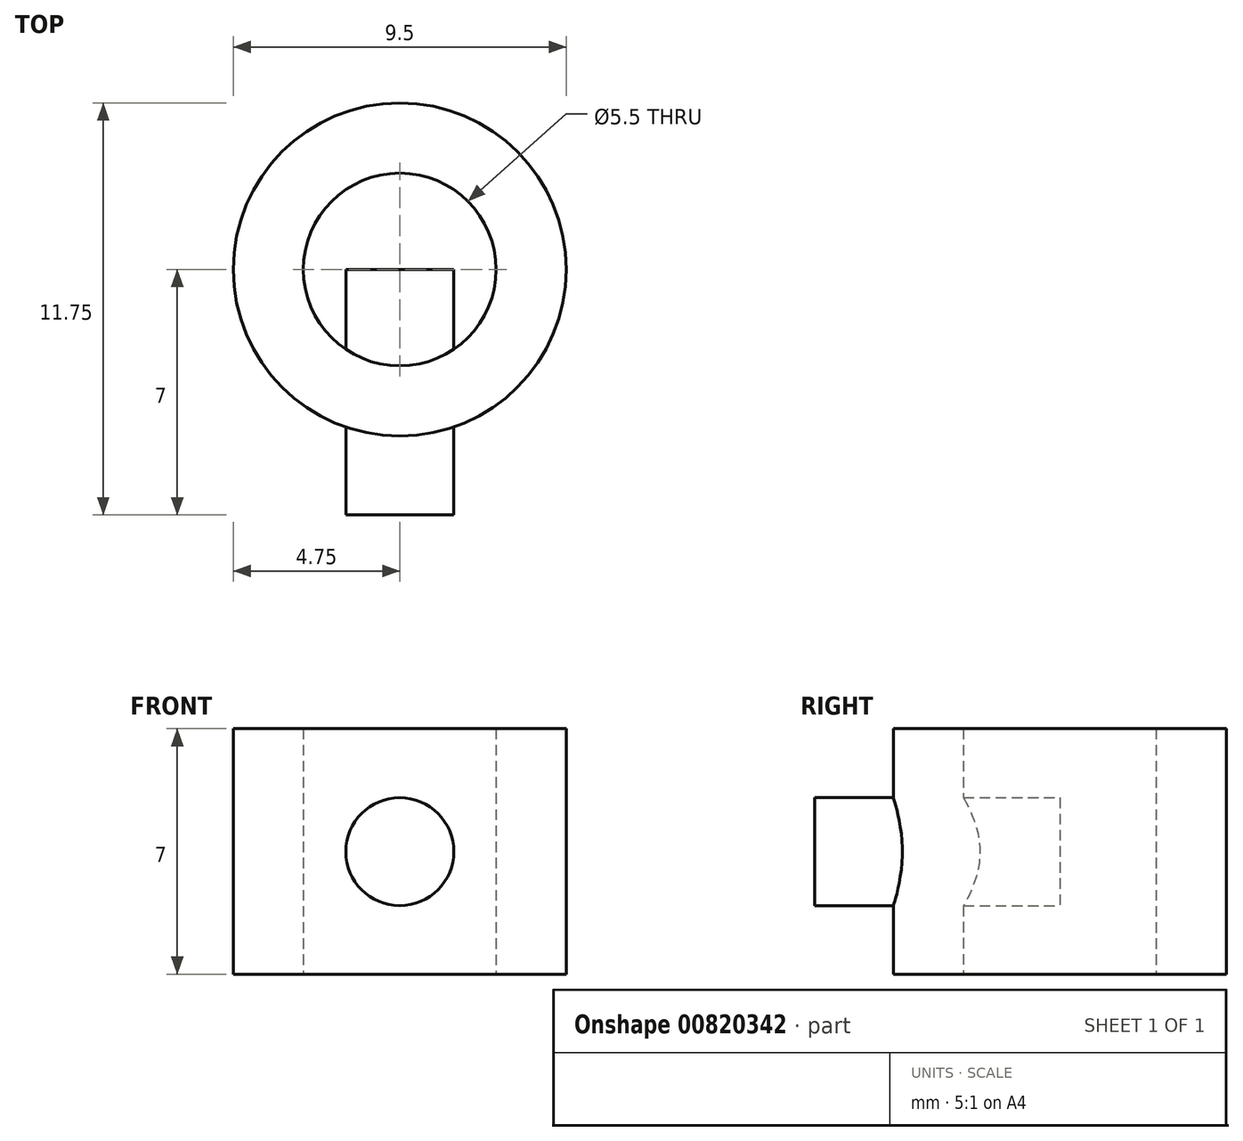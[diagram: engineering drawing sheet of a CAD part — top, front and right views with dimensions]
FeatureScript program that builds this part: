
annotation { "Feature Type Name" : "Feature", "Feature Type Description" : "" }
export const myFeature = defineFeature(function(context is Context, id is Id, definition is map)
    precondition{}
    {
        {
            var Q0;
            Q0=qCreatedBy(makeId("Top.planeOp"),FACE);
            var sketch = newSketch(context, id + "F0", { "sketchPlane" : qUnion([Q0])});
            skCircle(sketch, "E0", {"center": v(0, 0) * mm, "radius": 2.75 * mm});
            skCircle(sketch, "E1.0", {"center": v(0, 0) * mm, "radius": 4.75 * mm});
            skSolve(sketch);
        }
        {
            var Q0;
            Q0 = qSketchRegion(id + "F0", true);
            extrude(context, id + "F1", {"entities" : qUnion([Q0]), "depth" : 7 * mm, "offsetDistance" : 25 * mm});
        }
        {
            var Q0;
            Q0=qCreatedBy(makeId("Front.planeOp"),FACE);
            var sketch = newSketch(context, id + "F2", { "sketchPlane" : qUnion([Q0])});
            skCircle(sketch, "E2", {"center": v(0, 3.5) * mm, "radius": 1.54 * mm});
            skSolve(sketch);
        }
        {
            var Q0;
            Q0 = qSketchRegion(id + "F2", true);
            extrude(context, id + "F3", {"entities" : qUnion([Q0]), "operationType" : NewBodyOperationType.ADD, "depth" : 7 * mm, "offsetDistance" : 25 * mm});
        }
    });
